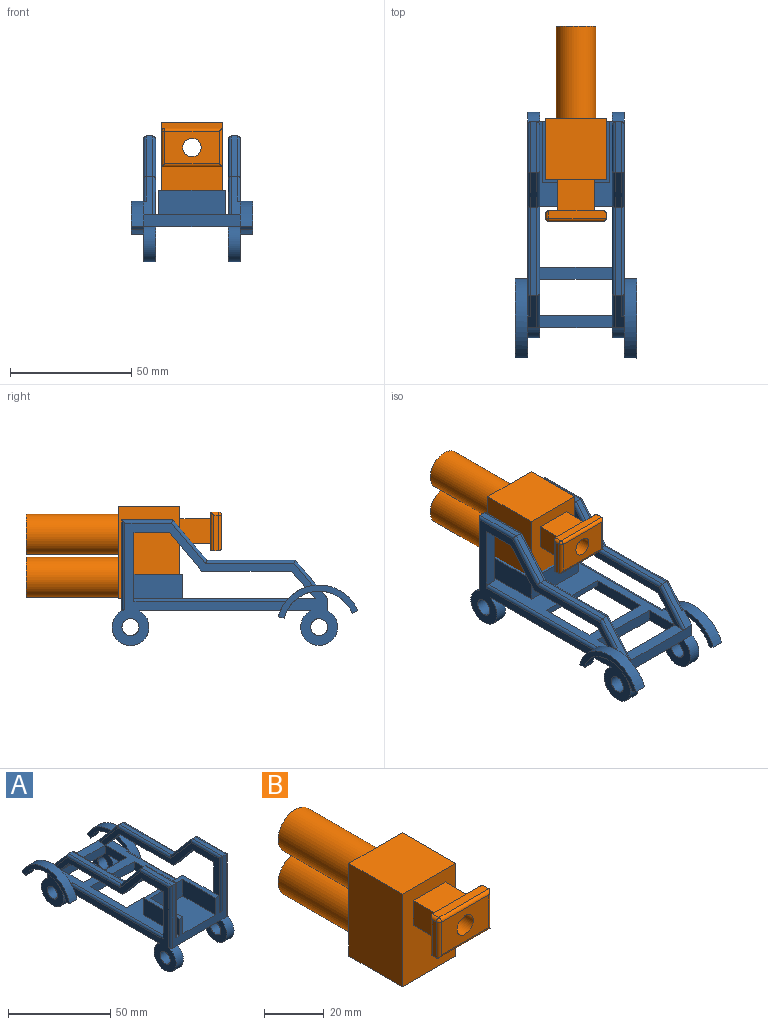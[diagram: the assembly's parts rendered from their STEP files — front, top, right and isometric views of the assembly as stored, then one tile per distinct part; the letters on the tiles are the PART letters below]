
ASSEMBLY  parts=2 mates=1
PART A: 95 faces, bbox 50x101.5x51.9 mm
  f0: plane 22.48x20.87mm, normal (-1,0,0), area 229.4mm2, adj f2,f5,f14,f29,f30,f52,f53,f70
  f1: plane 22.49x20.87mm, normal (1,0,0), area 229.5mm2, adj f2,f5,f14,f35,f36,f38,f39,f60
  f2: plane 80x40mm, normal (0,0,1), area 1104.1mm2, adj f0,f1,f7,f9,f11,f12,f16,f17
  f3: plane 32.5x5mm, normal (0,0,1), area 150.9mm2, adj f10,f14,f46,f56,f82,f88
  f4: plane 30x5mm, normal (0,0,-1), area 150mm2, adj f9,f10,f11,f14
  f5: plane 70.76x40mm, normal (0,0,-1), area 857.6mm2, adj f0,f1,f7,f9,f11,f12,f13,f15
  f6: plane 30x5mm, normal (0,0,-1), area 150mm2, adj f7,f8,f16,f17
  f7: plane 64.06x19.36mm, normal (-1,0,0), area 339.1mm2, adj f2,f5,f6,f8,f12,f20,f21,f33
  f8: plane 30x2.5mm, normal (0,1,0), area 75mm2, adj f6,f7,f16,f21
  f9: plane 24.06x19.36mm, normal (1,0,0), area 214.1mm2, adj f2,f4,f5,f10,f18,f29,f30
  f10: plane 30x5mm, normal (0,-1,0), area 150mm2, adj f3,f4,f9,f11
  f11: plane 24.06x19.36mm, normal (-1,0,0), area 214.1mm2, adj f2,f4,f5,f10,f18,f35,f36
  f12: plane 30x5mm, normal (0,-1,0), area 150mm2, adj f2,f5,f7,f16
  f13: plane 82.84x50.61mm, normal (1,0,0), area 780.3mm2, adj f5,f33,f34,f37,f38,f43,f44,f45
  f14: plane 40x5mm, normal (0,1,0), area 200mm2, adj f0,f1,f3,f4,f30,f36,f39,f52
  f15: plane 82.84x50.61mm, normal (-1,0,0), area 780.3mm2, adj f5,f31,f32,f47,f48,f53,f54,f55
  f16: plane 64.06x19.36mm, normal (1,0,0), area 339.1mm2, adj f2,f5,f6,f8,f12,f20,f21,f31
  f17: plane 37.5x37.5mm, normal (0,-1,0), area 400mm2, adj f2,f6,f19,f23,f24,f26,f27,f28
  f18: plane 30x5mm, normal (0,1,0), area 150mm2, adj f2,f5,f9,f11
  f19: plane 22.5x22.5mm, normal (0,0,1), area 506.2mm2, adj f17,f22,f23,f27
  f20: plane 30x2.5mm, normal (0,1,0), area 75mm2, adj f2,f7,f16,f21
  f21: plane 30x30mm, normal (0,0,-1), area 900mm2, adj f7,f8,f16,f20
  f22: plane 22.5x10mm, normal (0,-1,0), area 225mm2, adj f19,f23,f27,f28
  f23: plane 22.5x10mm, normal (-1,0,0), area 225mm2, adj f17,f19,f22,f28
  f24: plane 25x10mm, normal (1,0,0), area 250mm2, adj f2,f17,f25,f28
  f25: plane 27.5x10mm, normal (0,1,0), area 275mm2, adj f2,f24,f26,f28
  f26: plane 25x10mm, normal (-1,0,0), area 250mm2, adj f2,f17,f25,f28
  f27: plane 22.5x10mm, normal (1,0,0), area 225mm2, adj f17,f19,f22,f28
  f28: plane 27.5x25mm, normal (0,0,1), area 181.3mm2, adj f17,f22,f23,f24,f25,f26,f27
  f29: cylinder r=3.52mm len=7.05mm, axis (-1,0,0), area 110.7mm2, adj f0,f9
  f30: cylinder r=7.62mm len=15.24mm, axis (-1,0,0), area 202.3mm2, adj f0,f5,f9,f14
  f31: cylinder r=3.52mm len=7.05mm, axis (-1,0,0), area 110.7mm2, adj f15,f16
  f32: cylinder r=7.62mm len=15.24mm, axis (-1,0,0), area 202.7mm2, adj f5,f15,f16,f17,f73
  f33: cylinder r=3.53mm len=7.05mm, axis (1,0,0), area 110.8mm2, adj f7,f13
  f34: cylinder r=7.62mm len=15.24mm, axis (1,0,0), area 202.7mm2, adj f5,f7,f13,f17,f85
  f35: cylinder r=3.52mm len=7.05mm, axis (1,0,0), area 110.7mm2, adj f1,f11
  f36: cylinder r=7.62mm len=15.24mm, axis (1,0,0), area 202.3mm2, adj f1,f5,f11,f14
  f37: plane 37.14x5mm, normal (0,0,-1), area 185.7mm2, adj f13,f38,f45,f46
  f38: plane 11.43x10mm, normal (0,-0.75,-0.66), area 75.9mm2, adj f1,f2,f13,f37,f46,f58
  f39: plane 15.86x13.4mm, normal (0,0.76,0.65), area 61.1mm2, adj f1,f14,f40,f62,f64,f83,f88
  f40: plane 36.43x2.5mm, normal (0,0,1), area 91.1mm2, adj f39,f41,f84,f89
  f41: plane 16.64x14.1mm, normal (0,0.76,0.65), area 54.5mm2, adj f40,f42,f86,f90
  f42: plane 21.07x2.5mm, normal (0,0,1), area 52.7mm2, adj f17,f41,f87,f91
  f43: plane 28.57x5mm, normal (0,1,0), area 136.9mm2, adj f2,f13,f44,f46,f93
  f44: plane 14.64x5mm, normal (0,0,-1), area 73.2mm2, adj f13,f43,f45,f46
  f45: plane 15.89x13.21mm, normal (0,-0.77,-0.64), area 103.3mm2, adj f13,f37,f44,f46
  f46: plane 82.11x31.25mm, normal (-1,0,0), area 409.3mm2, adj f2,f3,f37,f38,f43,f44,f45,f88
  f47: plane 14.64x5mm, normal (0,0,-1), area 73.2mm2, adj f15,f48,f55,f56
  f48: plane 28.57x5mm, normal (0,1,0), area 136.9mm2, adj f2,f15,f47,f56,f94
  f49: plane 21.07x2.5mm, normal (0,0,1), area 52.7mm2, adj f17,f50,f74,f79
  f50: plane 16.64x14.1mm, normal (0,0.76,0.65), area 54.5mm2, adj f49,f51,f75,f80
  f51: plane 36.43x2.5mm, normal (0,0,1), area 91.1mm2, adj f50,f52,f76,f81
  f52: plane 15.86x13.4mm, normal (0,0.76,0.65), area 61.1mm2, adj f0,f14,f51,f66,f68,f77,f82
  f53: plane 11.43x10mm, normal (0,-0.75,-0.66), area 75.9mm2, adj f0,f2,f15,f54,f56,f65
  f54: plane 37.14x5mm, normal (0,0,-1), area 185.7mm2, adj f15,f53,f55,f56
  f55: plane 15.89x13.21mm, normal (0,-0.77,-0.64), area 103.3mm2, adj f15,f47,f54,f56
  f56: plane 82.11x31.25mm, normal (1,0,0), area 409.3mm2, adj f2,f3,f47,f48,f53,f54,f55,f78
  f57: plane 3.57x3.06mm, normal (-1,0,0), area 7.3mm2, adj f5,f59,f60,f62
  f58: plane 9.04x4.71mm, normal (-1,0,0), area 18.5mm2, adj f2,f38,f60,f62
  f59: plane 5x2.42mm, normal (0,-0.25,-0.97), area 12.5mm2, adj f57,f60,f62,f63
  f60: cylinder r=14.87mm len=28.1mm, axis (-1,0,0), area 185.3mm2, adj f1,f57,f58,f59,f61,f63,f64
  f61: plane 5x2.3mm, normal (0,0.39,-0.92), area 12.5mm2, adj f60,f62,f63,f64
  f62: cylinder r=17.37mm len=32.83mm, axis (-1,0,0), area 217.3mm2, adj f2,f13,f39,f57,f58,f59,f61,f63
  f63: plane 32.83x13.69mm, normal (1,0,0), area 100.4mm2, adj f59,f60,f61,f62
  f64: plane 17.17x11.6mm, normal (-1,0,0), area 47.6mm2, adj f39,f60,f61,f62
  f65: plane 9.05x4.71mm, normal (1,0,0), area 18.6mm2, adj f2,f53,f68,f70
  f66: plane 17.17x11.6mm, normal (1,0,0), area 47.7mm2, adj f52,f68,f69,f70
  f67: plane 5x2.42mm, normal (0,-0.25,-0.97), area 12.5mm2, adj f68,f70,f71,f72
  f68: cylinder r=17.37mm len=32.83mm, axis (1,0,0), area 217.3mm2, adj f2,f15,f52,f65,f66,f67,f69,f71
  f69: plane 5x2.3mm, normal (0,0.39,-0.92), area 12.5mm2, adj f66,f68,f70,f71
  f70: cylinder r=14.87mm len=28.1mm, axis (1,0,0), area 185.2mm2, adj f0,f65,f66,f67,f69,f71,f72
  f71: plane 32.83x13.69mm, normal (-1,0,0), area 100.7mm2, adj f67,f68,f69,f70
  f72: plane 3.58x3.06mm, normal (1,0,0), area 7.3mm2, adj f5,f67,f68,f70
  f73: cylinder r=1.25mm len=37.5mm, axis (0,0,1), area 72.3mm2, adj f15,f17,f32,f74
  f74: cylinder r=1.25mm len=21.07mm, axis (0,1,0), area 40.1mm2, adj f15,f49,f73,f75
  f75: cylinder r=1.25mm len=17.89mm, axis (0,0.65,-0.76), area 42.8mm2, adj f15,f50,f74,f76
  f76: cylinder r=1.25mm len=37.01mm, axis (0,1,0), area 71.5mm2, adj f15,f51,f75,f77
  f77: cylinder r=1.25mm len=11.08mm, axis (0,0.65,-0.76), area 25.4mm2, adj f15,f52,f68,f76
  f78: cylinder r=1.25mm len=32.5mm, axis (0,0,1), area 62.9mm2, adj f2,f17,f56,f79
  f79: cylinder r=1.25mm len=21.07mm, axis (0,-1,0), area 40.1mm2, adj f49,f56,f78,f80
  f80: cylinder r=1.25mm len=17.89mm, axis (0,-0.65,0.76), area 42.8mm2, adj f50,f56,f79,f81
  f81: cylinder r=1.25mm len=37.01mm, axis (0,-1,0), area 71.5mm2, adj f51,f56,f80,f82
  f82: cylinder r=1.25mm len=16.67mm, axis (0,-0.65,0.76), area 39.6mm2, adj f3,f52,f56,f81
  f83: cylinder r=1.25mm len=11.08mm, axis (0,0.65,-0.76), area 25.4mm2, adj f13,f39,f62,f84
  f84: cylinder r=1.25mm len=37.01mm, axis (0,1,0), area 71.5mm2, adj f13,f40,f83,f86
  f85: cylinder r=1.25mm len=37.5mm, axis (0,0,-1), area 72.3mm2, adj f13,f17,f34,f87
  f86: cylinder r=1.25mm len=17.89mm, axis (0,0.65,-0.76), area 42.8mm2, adj f13,f41,f84,f87
  f87: cylinder r=1.25mm len=21.07mm, axis (0,1,0), area 40.1mm2, adj f13,f42,f85,f86
  f88: cylinder r=1.25mm len=16.67mm, axis (0,0.65,-0.76), area 39.6mm2, adj f3,f39,f46,f89
  f89: cylinder r=1.25mm len=37.01mm, axis (0,1,0), area 71.5mm2, adj f40,f46,f88,f90
  f90: cylinder r=1.25mm len=17.89mm, axis (0,0.65,-0.76), area 42.8mm2, adj f41,f46,f89,f91
  f91: cylinder r=1.25mm len=21.07mm, axis (0,1,0), area 40.1mm2, adj f42,f46,f90,f92
  f92: cylinder r=1.25mm len=32.5mm, axis (0,0,1), area 62.9mm2, adj f2,f17,f46,f91
  f93: cylinder r=1.25mm len=63.64mm, axis (0,-1,0), area 124.2mm2, adj f2,f13,f43,f62
  f94: cylinder r=1.25mm len=63.64mm, axis (0,1,0), area 124.2mm2, adj f2,f15,f48,f68
PART B: 38 faces, bbox 25.4x80.6x38.1 mm
  f0: plane 38.1x25.4mm, normal (0,1,0), area 539.6mm2, adj f9,f10,f11,f12,f34,f36
  f1: plane 38.1x25.4mm, normal (0,-1,0), area 812.9mm2, adj f9,f10,f11,f12,f15,f16,f17,f18
  f2: plane 15.24x15.24mm, normal (0,0,1), area 222.5mm2, adj f3,f4,f5,f6,f14
  f3: plane 30.48x15.24mm, normal (0,-1,0), area 229.2mm2, adj f2,f4,f6,f7,f8,f13
  f4: plane 30.48x15.24mm, normal (1,0,0), area 464.5mm2, adj f2,f3,f5,f7
  f5: plane 30.48x15.24mm, normal (0,1,0), area 418.9mm2, adj f2,f4,f6,f7,f19
  f6: plane 30.48x15.24mm, normal (-1,0,0), area 464.5mm2, adj f2,f3,f5,f7
  f7: plane 15.24x15.24mm, normal (0,0,-1), area 232.3mm2, adj f3,f4,f5,f6
  f8: cylinder r=6.35mm len=43.18mm, axis (0,1,0), area 1722.8mm2, adj f3,f35
  f9: plane 38.1x25.4mm, normal (1,0,0), area 967.7mm2, adj f0,f1,f11,f12
  f10: plane 38.1x25.4mm, normal (-1,0,0), area 967.7mm2, adj f0,f1,f11,f12
  f11: plane 25.4x25.4mm, normal (0,0,-1), area 645.2mm2, adj f0,f1,f9,f10
  f12: plane 25.4x25.4mm, normal (0,0,1), area 645.2mm2, adj f0,f1,f9,f10
  f13: cylinder r=6.35mm len=43.18mm, axis (0,1,0), area 1722.8mm2, adj f3,f14,f37
  f14: cone r=0mm half-angle=59deg, axis (0,1,0), area 21mm2, adj f2,f13
  f15: plane 15.24x12.7mm, normal (0,0,1), area 193.5mm2, adj f1,f16,f18,f20
  f16: plane 12.7x10.16mm, normal (-1,0,0), area 129mm2, adj f1,f15,f17,f20
  f17: plane 15.24x12.7mm, normal (0,0,-1), area 193.5mm2, adj f1,f16,f18,f20
  f18: plane 12.7x10.16mm, normal (1,0,0), area 129mm2, adj f1,f15,f17,f20
  f19: cylinder r=3.81mm len=22.23mm, axis (0,-1,0), area 532mm2, adj f5,f21
  f20: plane 22.46x16mm, normal (0,1,0), area 204.5mm2, adj f15,f16,f17,f18,f23,f25,f31,f33
  f21: plane 22.46x13.46mm, normal (0,-1,0), area 256.7mm2, adj f19,f26,f27,f28,f29
  f22: plane 16x1.91mm, normal (1,0,0), area 30.5mm2, adj f23,f25,f26,f33
  f23: plane 25x3.18mm, normal (0,0,-1), area 78.7mm2, adj f20,f22,f24,f27,f31,f33
  f24: plane 14.73x1.91mm, normal (-1,0,0), area 28.1mm2, adj f23,f29,f31,f32
  f25: plane 23.73x3.18mm, normal (0,0,1), area 75mm2, adj f20,f22,f28,f32,f33
  f26: cylinder r=1.27mm len=16mm, axis (0,0,-1), area 30.1mm2, adj f21,f22,f27,f28
  f27: cylinder r=1.27mm len=25mm, axis (-1,0,0), area 48mm2, adj f21,f23,f26,f29
  f28: cylinder r=1.27mm len=23.73mm, axis (1,0,0), area 46.4mm2, adj f21,f25,f26,f30
  f29: cylinder r=1.27mm len=14.73mm, axis (0,0,1), area 28.5mm2, adj f21,f24,f27,f30
  f30: sphere r=1.27mm, area 2.5mm2, adj f28,f29,f32
  f31: cylinder r=1.27mm len=16mm, axis (0,0,-1), area 31mm2, adj f20,f23,f24,f32
  f32: cylinder r=1.27mm len=3.18mm, axis (0,1,0), area 5.4mm2, adj f24,f25,f30,f31
  f33: cylinder r=1.27mm len=16mm, axis (0,0,1), area 31.9mm2, adj f20,f22,f23,f25
  f34: cylinder r=8.26mm len=38.1mm, axis (0,-1,0), area 1976.2mm2, adj f0,f35
  f35: plane 16.51x16.51mm, normal (0,1,0), area 87.4mm2, adj f8,f34
  f36: cylinder r=8.26mm len=38.1mm, axis (0,-1,0), area 1976.2mm2, adj f0,f37
  f37: plane 16.51x16.51mm, normal (0,1,0), area 87.4mm2, adj f13,f36
PLACE A rot(axis=(0,0,1),180deg) t=(-99.71,-40.89,46.28)mm
PLACE B rot(axis=(-0.93,-0.35,-0.08),0deg) t=(-99.71,-9.64,51.28)mm
MATE fastened A.f19 <-> B.f11  axis (0,0,1) through (-99.71,-9.64,51.28)mm
